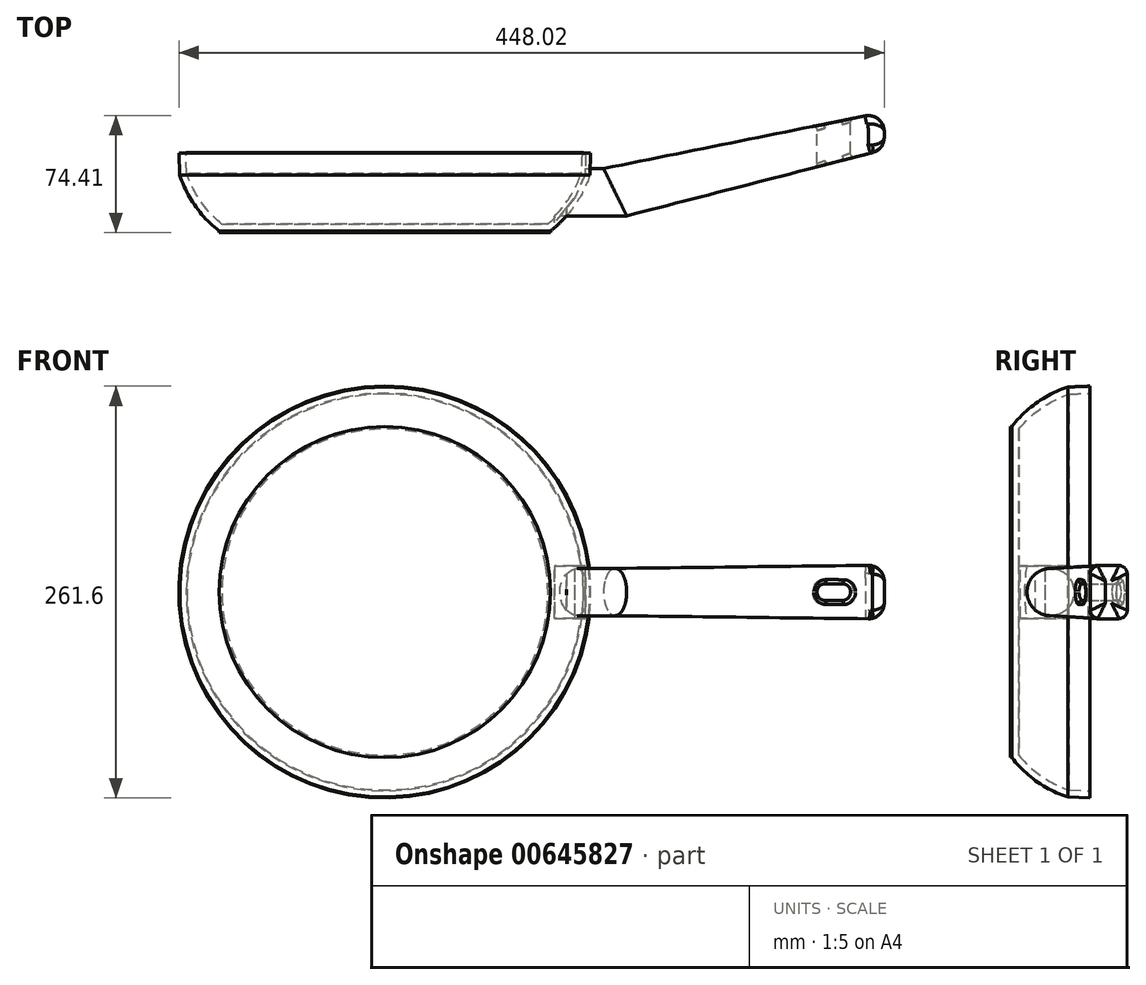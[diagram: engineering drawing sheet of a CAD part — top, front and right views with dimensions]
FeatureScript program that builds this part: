
annotation { "Feature Type Name" : "Feature", "Feature Type Description" : "" }
export const myFeature = defineFeature(function(context is Context, id is Id, definition is map)
    precondition{}
    {
        {
            var Q0;
            Q0=qCreatedBy(makeId("Top.planeOp"),FACE);
            var sketch = newSketch(context, id + "F0", { "sketchPlane" : qUnion([Q0])});
            skLineSegment(sketch, "E0", {"start": v(-53.22, -24.7) * mm, "end": v(0, -24.7) * mm});
            skLineSegment(sketch, "E1.MirrorCS", {"start": v(77.58, 25) * mm, "end": v(77, 10.88) * mm});
            skArc(sketch, "E2.MirrorCS", {"start": v(77, 10.88) * mm, "mid": v(67.12, -8.77) * mm, "end": v(51.94, -24.7) * mm});
            skLineSegment(sketch, "E3.MirrorCS", {"start": v(51.94, -24.7) * mm, "end": v(0, -24.7) * mm});
            skLineSegment(sketch, "E4", {"start": v(-53.22, 25.92) * mm, "end": v(-53.22, -24.7) * mm});
            skLineSegment(sketch, "E5", {"start": v(-53.22, 25.92) * mm, "end": v(77.58, 25) * mm});
            skSolve(sketch);
        }
        {
            var Q0;
            Q0=makeQuery(id+"F0.imprint","IMPRINT",FACE,{"disambiguationData":[TD([[makeQuery(id+"F0.imprint","IMPRINT",EDGE,{"derivedFrom":sQuery(id+"F0.wireOp",EDGE,"E0")}),1.0]])]});
            var Q1;
            Q1=sQuery(id+"F0.wireOp",EDGE,"E4");
            revolve(context, id + "F1", {"entities" : qUnion([Q0]), "axis" : qUnion([Q1]), "revolveType" : RevolveType.FULL});
        }
        {
            var Q0;
            Q0=makeQuery(id+"F1.opRevolve","SWEPT_FACE",FACE,{"disambiguationData":[OSD([sQuery(id+"F0.wireOp",EDGE,"E5")])]});
            shell(context, id + "F2", {"entities" : qUnion([Q0]), "thickness" : 4.5 * mm});
        }
        {
            var Q0;
            Q0=qCreatedBy(makeId("Right.planeOp"),FACE);
            cPlane(context, id + "F3", {"entities" : qUnion([Q0]), "cplaneType" : CPlaneType.OFFSET, "offset" : 72.9 * mm, "width" : 150 * mm, "height" : 150 * mm});
        }
        {
            var Q0;
            Q0=qCreatedBy(id+"F3.planeOp",FACE);
            var sketch = newSketch(context, id + "F4", { "sketchPlane" : qUnion([Q0])});
            skCircle(sketch, "E6", {"center": v(0, 0) * mm, "radius": 15 * mm});
            skSolve(sketch);
        }
        {
            var Q0;
            Q0=makeQuery(id+"F4.imprint","IMPRINT",FACE,{"disambiguationData":[TD([[makeQuery(id+"F4.imprint","IMPRINT",EDGE,{"derivedFrom":sQuery(id+"F4.wireOp",EDGE,"E6")}),1.0]])]});
            extrude(context, id + "F5", {"entities" : qUnion([Q0]), "endBound" : BoundingType.SYMMETRIC, "oppositeDirection" : true, "depth" : 57.8 * mm, "offsetDistance" : 25 * mm});
        }
        {
            var Q0;
            Q0=makeQuery(id+"F5.opExtrude","CAP_FACE",FACE,{"disambiguationData":[OSD([sQuery(id+"F4.wireOp",EDGE,"E6")])],"isStart":false});
            extrude(context, id + "F6", {"entities" : qUnion([Q0]), "operationType" : NewBodyOperationType.REMOVE, "oppositeDirection" : true, "depth" : 18.3 * mm, "offsetDistance" : 25 * mm});
        }
        {
            var Q0;
            Q0=qCreatedBy(makeId("Top.planeOp"),FACE);
            cPlane(context, id + "F7", {"entities" : qUnion([Q0]), "cplaneType" : CPlaneType.OFFSET, "offset" : 0 * mm, "width" : 150 * mm, "height" : 150 * mm});
        }
        {
            var Q0;
            Q0=qCreatedBy(id+"F7.planeOp",FACE);
            var sketch = newSketch(context, id + "F8", { "sketchPlane" : qUnion([Q0])});
            skLineSegment(sketch, "E7", {"start": v(74.17, 24.08) * mm, "end": v(74.17, 11.67) * mm});
            skLineSegment(sketch, "E8", {"start": v(74.17, 11.67) * mm, "end": v(67.43, -3.3) * mm});
            skLineSegment(sketch, "E9", {"start": v(67.43, -3.3) * mm, "end": v(54.48, -19.24) * mm});
            skLineSegment(sketch, "E10", {"start": v(54.48, -19.24) * mm, "end": v(54.48, 24.66) * mm});
            skLineSegment(sketch, "E11", {"start": v(54.48, 24.66) * mm, "end": v(74.17, 24.08) * mm});
            skSolve(sketch);
        }
        {
            var Q0;
            Q0=makeQuery(id+"F8.imprint","IMPRINT",FACE,{"disambiguationData":[TD([[makeQuery(id+"F8.imprint","IMPRINT",EDGE,{"derivedFrom":sQuery(id+"F8.wireOp",EDGE,"E7")}),-1.0]])]});
            extrude(context, id + "F9", {"entities" : qUnion([Q0]), "operationType" : NewBodyOperationType.REMOVE, "endBound" : BoundingType.SYMMETRIC, "oppositeDirection" : true, "depth" : 33.2 * mm, "offsetDistance" : 25 * mm});
        }
        {
            var Q0;
            Q0=qCreatedBy(makeId("Top.planeOp"),FACE);
            var sketch = newSketch(context, id + "F10", { "sketchPlane" : qUnion([Q0])});
            skLineSegment(sketch, "E12", {"start": v(84.38, 17.8) * mm, "end": v(107.07, 17.8) * mm});
            skLineSegment(sketch, "E13", {"start": v(84.38, 17.8) * mm, "end": v(103.59, -21.57) * mm});
            skLineSegment(sketch, "E14", {"start": v(103.59, -21.57) * mm, "end": v(107.07, 17.8) * mm});
            skSolve(sketch);
        }
        {
            var Q0;
            Q0=qCreatedBy(makeId("Right.planeOp"),FACE);
            cPlane(context, id + "F11", {"entities" : qUnion([Q0]), "cplaneType" : CPlaneType.OFFSET, "offset" : 264 * mm, "width" : 150 * mm, "height" : 150 * mm});
        }
        {
            var Q0;
            Q0=makeQuery(id+"F10.imprint","IMPRINT",FACE,{"disambiguationData":[TD([[makeQuery(id+"F10.imprint","IMPRINT",EDGE,{"derivedFrom":sQuery(id+"F10.wireOp",EDGE,"E12")}),-1.0]])]});
            extrude(context, id + "F12", {"entities" : qUnion([Q0]), "operationType" : NewBodyOperationType.REMOVE, "endBound" : BoundingType.SYMMETRIC, "oppositeDirection" : true, "depth" : 34.2 * mm, "offsetDistance" : 25 * mm});
        }
        {
            var Q0;
            Q0=qCreatedBy(id+"F11.planeOp",FACE);
            var sketch = newSketch(context, id + "F13", { "sketchPlane" : qUnion([Q0])});
            skLineSegment(sketch, "E15.bottom", {"start": v(45.94, -17.1) * mm, "end": v(32.04, -17.1) * mm});
            skLineSegment(sketch, "E15.top", {"start": v(45.94, 17.1) * mm, "end": v(32.04, 17.1) * mm});
            skLineSegment(sketch, "E15.left", {"start": v(50.94, -12.1) * mm, "end": v(50.94, 12.1) * mm});
            skLineSegment(sketch, "E15.right", {"start": v(27.04, -12.1) * mm, "end": v(27.04, 12.1) * mm});
            skPoint(sketch, "E15.middle", {"position": v(38.99, 0) * mm});
            skPoint(sketch, "E16.visualSharp", {"position": v(50.94, 17.1) * mm});
            skArc(sketch, "E16.filletArc", {"start": v(50.94, 12.1) * mm, "mid": v(49.48, 15.64) * mm, "end": v(45.94, 17.1) * mm});
            skPoint(sketch, "E17.visualSharp", {"position": v(50.94, -17.1) * mm});
            skArc(sketch, "E17.filletArc", {"start": v(45.94, -17.1) * mm, "mid": v(49.48, -15.64) * mm, "end": v(50.94, -12.1) * mm});
            skPoint(sketch, "E18.visualSharp", {"position": v(27.04, -17.1) * mm});
            skArc(sketch, "E18.filletArc", {"start": v(27.04, -12.1) * mm, "mid": v(28.5, -15.64) * mm, "end": v(32.04, -17.1) * mm});
            skPoint(sketch, "E19.visualSharp", {"position": v(27.04, 17.1) * mm});
            skArc(sketch, "E19.filletArc", {"start": v(32.04, 17.1) * mm, "mid": v(28.5, 15.64) * mm, "end": v(27.04, 12.1) * mm});
            skSolve(sketch);
        }
        {
            var Q0;
            Q0=makeQuery(id+"F1.opRevolve","SWEPT_FACE",FACE,{"disambiguationData":[OSD([sQuery(id+"F0.wireOp",EDGE,"E0"),sQuery(id+"F0.wireOp",EDGE,"E3.MirrorCS")])]});
            extrude(context, id + "F14", {"entities" : qUnion([Q0]), "depth" : 1 * mm, "offsetDistance" : 25 * mm});
        }
        {
            var Q1;
            Q1=makeQuery(id+"F12.boolean.opBoolean","COPY",FACE,{"derivedFrom":makeQuery(id+"F12.opExtrude","SWEPT_FACE",FACE,{"disambiguationData":[OSD([sQuery(id+"F10.wireOp",EDGE,"E13")])]})});
            var Q2;
            Q2=makeQuery(id+"F13.imprint","IMPRINT",FACE,{"disambiguationData":[TD([[makeQuery(id+"F13.imprint","IMPRINT",EDGE,{"derivedFrom":sQuery(id+"F13.wireOp",EDGE,"E15.bottom")}),-1.0]])]});
            loft(context, id + "F15", {"operationType" : NewBodyOperationType.ADD, "sheetProfilesArray" : [{ "sheetProfileEntities" : qUnion([Q1]) }, { "sheetProfileEntities" : qUnion([Q2]) }]});
        }
        {
            var Q0;
            Q0=makeQuery(id+"F15.opLoft","MID_CAP_EDGE",EDGE,{"disambiguationData":[OSD([sQuery(id+"F13.wireOp",EDGE,"E15.left"),sQuery(id+"F13.wireOp",EDGE,"E16.filletArc"),sQuery(id+"F13.wireOp",EDGE,"E17.filletArc")])],"capPos":1.0});
            var Q1;
            Q1=makeQuery(id+"F15.opLoft","CAP_FACE",FACE,{"disambiguationData":[OSD([makeQuery(id+"F13.imprint","IMPRINT",FACE,{"disambiguationData":[TD([[makeQuery(id+"F13.imprint","IMPRINT",EDGE,{"derivedFrom":sQuery(id+"F13.wireOp",EDGE,"E15.bottom")}),-1.0]])]})])],"isStart":true});
            fillet(context, id + "F16", {"entities" : qUnion([Q0, Q1]), "radius" : 10.06 * mm, "tangentPropagation" : true, "allowEdgeOverflow" : false});
        }
        {
            var Q0;
            Q0=qCreatedBy(makeId("Front.planeOp"),FACE);
            cPlane(context, id + "F17", {"entities" : qUnion([Q0]), "cplaneType" : CPlaneType.OFFSET, "offset" : 65 * mm, "oppositeDirection" : true, "width" : 150 * mm, "height" : 150 * mm});
        }
        {
            var Q0;
            Q0=qCreatedBy(id+"F17.planeOp",FACE);
            var sketch = newSketch(context, id + "F18", { "sketchPlane" : qUnion([Q0])});
            skLineSegment(sketch, "E20.bottom", {"start": v(226.34, 5.27) * mm, "end": v(237.54, 5.27) * mm});
            skLineSegment(sketch, "E20.top", {"start": v(226.34, -5.27) * mm, "end": v(237.54, -5.27) * mm});
            skLineSegment(sketch, "E20.left", {"start": v(221.34, 0.27) * mm, "end": v(221.34, -0.27) * mm});
            skLineSegment(sketch, "E20.right", {"start": v(242.54, 0.27) * mm, "end": v(242.54, -0.27) * mm});
            skPoint(sketch, "E20.middle", {"position": v(231.94, 0) * mm});
            skPoint(sketch, "E21.visualSharp", {"position": v(242.54, 5.27) * mm});
            skArc(sketch, "E21.filletArc", {"start": v(242.54, 0.27) * mm, "mid": v(241.08, 3.8) * mm, "end": v(237.54, 5.27) * mm});
            skPoint(sketch, "E22.visualSharp", {"position": v(242.54, -5.27) * mm});
            skArc(sketch, "E22.filletArc", {"start": v(237.54, -5.27) * mm, "mid": v(241.08, -3.8) * mm, "end": v(242.54, -0.27) * mm});
            skPoint(sketch, "E23.visualSharp", {"position": v(221.34, -5.27) * mm});
            skArc(sketch, "E23.filletArc", {"start": v(221.34, -0.27) * mm, "mid": v(222.8, -3.8) * mm, "end": v(226.34, -5.27) * mm});
            skPoint(sketch, "E24.visualSharp", {"position": v(221.34, 5.27) * mm});
            skArc(sketch, "E24.filletArc", {"start": v(226.34, 5.27) * mm, "mid": v(222.8, 3.8) * mm, "end": v(221.34, 0.27) * mm});
            skSolve(sketch);
        }
        {
            var Q0;
            Q0=makeQuery(id+"F18.imprint","IMPRINT",FACE,{"disambiguationData":[TD([[makeQuery(id+"F18.imprint","IMPRINT",EDGE,{"derivedFrom":sQuery(id+"F18.wireOp",EDGE,"E20.bottom")}),-1.0]])]});
            extrude(context, id + "F19", {"entities" : qUnion([Q0]), "operationType" : NewBodyOperationType.REMOVE, "depth" : 115 * mm, "offsetDistance" : 25 * mm});
        }
        {
            var Q0;
            Q0=makeQuery(id+"F19.boolean.opBoolean","INTERSECT",EDGE,{"disambiguationData":[OD(1.0)],"derivedFrom":[makeQuery(id+"F15.opLoft","SWEPT_FACE",FACE,{"disambiguationData":[OSD([sQuery(id+"F4.wireOp",EDGE,"E6"),sQuery(id+"F10.wireOp",EDGE,"E13"),sQuery(id+"F13.wireOp",EDGE,"E15.bottom"),sQuery(id+"F13.wireOp",EDGE,"E15.right"),sQuery(id+"F13.wireOp",EDGE,"E17.filletArc"),sQuery(id+"F13.wireOp",EDGE,"E18.filletArc")])]}),makeQuery(id+"F19.opExtrude","SWEPT_FACE",FACE,{"disambiguationData":[OSD([sQuery(id+"F18.wireOp",EDGE,"E20.bottom")])]})]});
            var Q1;
            Q1=makeQuery(id+"F19.boolean.opBoolean","INTERSECT",EDGE,{"disambiguationData":[OD(0.0)],"derivedFrom":[makeQuery(id+"F15.opLoft","SWEPT_FACE",FACE,{"disambiguationData":[OSD([sQuery(id+"F4.wireOp",EDGE,"E6"),sQuery(id+"F10.wireOp",EDGE,"E13"),sQuery(id+"F13.wireOp",EDGE,"E15.bottom"),sQuery(id+"F13.wireOp",EDGE,"E15.right"),sQuery(id+"F13.wireOp",EDGE,"E17.filletArc"),sQuery(id+"F13.wireOp",EDGE,"E18.filletArc")])]}),makeQuery(id+"F19.opExtrude","SWEPT_FACE",FACE,{"disambiguationData":[OSD([sQuery(id+"F18.wireOp",EDGE,"E20.top")])]})]});
            fillet(context, id + "F20", {"entities" : qUnion([Q0, Q1]), "radius" : 2.54 * mm, "tangentPropagation" : true, "allowEdgeOverflow" : false});
        }
    });
